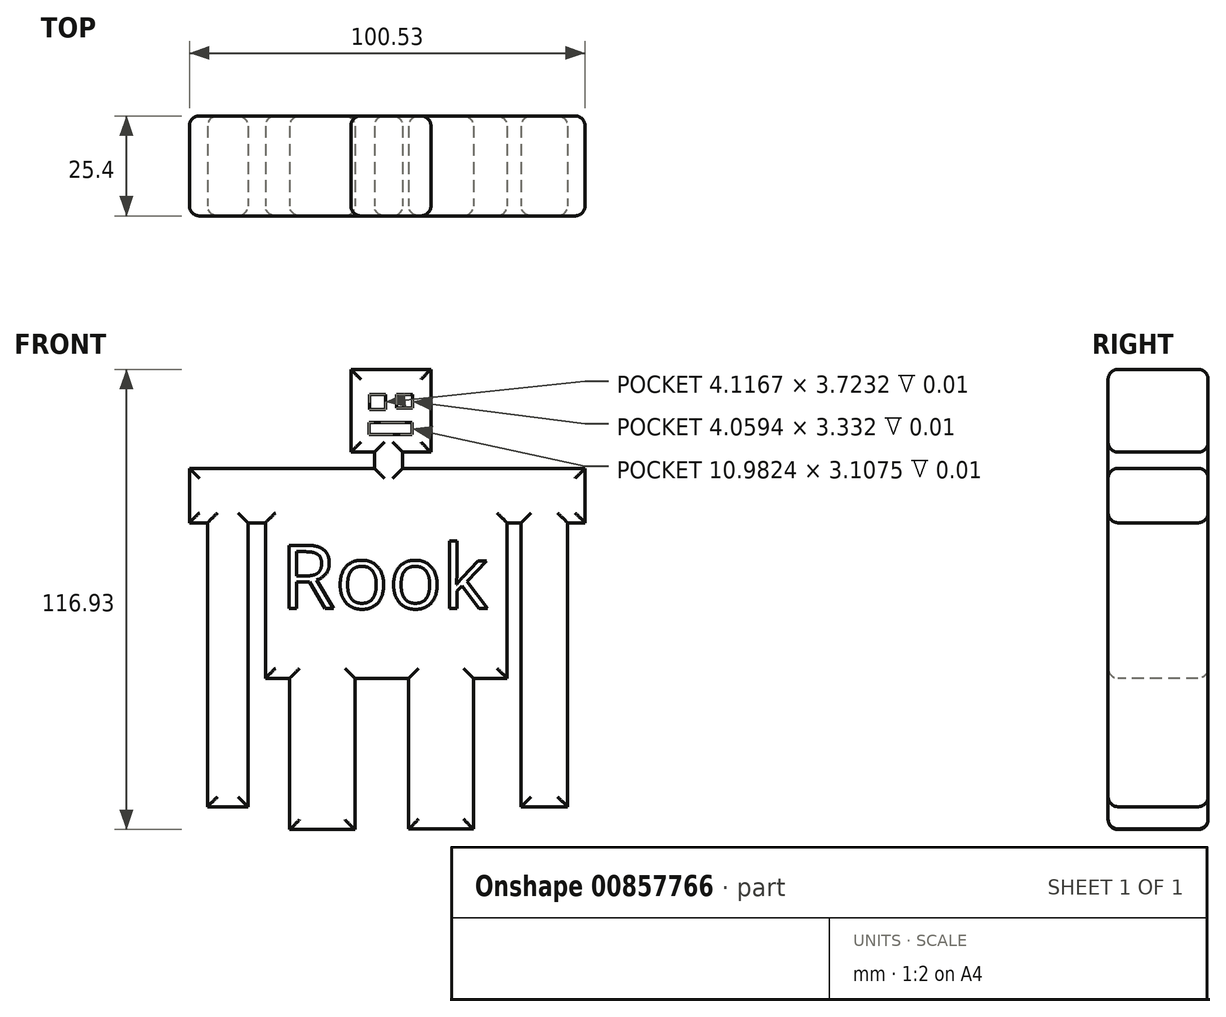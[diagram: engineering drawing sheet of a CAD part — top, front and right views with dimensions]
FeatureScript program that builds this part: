
annotation { "Feature Type Name" : "Feature", "Feature Type Description" : "" }
export const myFeature = defineFeature(function(context is Context, id is Id, definition is map)
    precondition{}
    {
        {
            var Q0;
            Q0=qCreatedBy(makeId("Front.planeOp"),FACE);
            var sketch = newSketch(context, id + "F0", { "sketchPlane" : qUnion([Q0])});
            skLineSegment(sketch, "E0.bottom", {"start": v(-8.8, 63.85) * mm, "end": v(11.54, 63.85) * mm});
            skLineSegment(sketch, "E0.top", {"start": v(-8.8, 42.83) * mm, "end": v(11.54, 42.83) * mm});
            skLineSegment(sketch, "E0.left", {"start": v(-8.8, 63.85) * mm, "end": v(-8.8, 42.83) * mm});
            skLineSegment(sketch, "E0.right", {"start": v(11.54, 63.85) * mm, "end": v(11.54, 42.83) * mm});
            skLineSegment(sketch, "E1.bottom", {"start": v(-2.82, 42.83) * mm, "end": v(4.36, 42.83) * mm});
            skLineSegment(sketch, "E1.top", {"start": v(-2.82, 38.72) * mm, "end": v(4.36, 38.72) * mm});
            skLineSegment(sketch, "E1.left", {"start": v(-2.82, 42.83) * mm, "end": v(-2.82, 38.72) * mm});
            skLineSegment(sketch, "E1.right", {"start": v(4.36, 42.83) * mm, "end": v(4.36, 38.72) * mm});
            skLineSegment(sketch, "E2.bottom", {"start": v(-30.52, 38.72) * mm, "end": v(30.86, 38.72) * mm});
            skLineSegment(sketch, "E2.top", {"start": v(-30.52, -14.62) * mm, "end": v(30.86, -14.62) * mm});
            skLineSegment(sketch, "E2.left", {"start": v(-30.52, 38.72) * mm, "end": v(-30.52, -14.62) * mm});
            skLineSegment(sketch, "E2.right", {"start": v(30.86, 38.72) * mm, "end": v(30.86, -14.62) * mm});
            skLineSegment(sketch, "E3.bottom", {"start": v(30.86, 38.72) * mm, "end": v(50.7, 38.72) * mm});
            skLineSegment(sketch, "E3.top", {"start": v(30.86, 24.87) * mm, "end": v(50.7, 24.87) * mm});
            skLineSegment(sketch, "E3.left", {"start": v(30.86, 38.72) * mm, "end": v(30.86, 24.87) * mm});
            skLineSegment(sketch, "E3.right", {"start": v(50.7, 38.72) * mm, "end": v(50.7, 24.87) * mm});
            skLineSegment(sketch, "E4.bottom", {"start": v(34.45, 24.87) * mm, "end": v(46.25, 24.87) * mm});
            skLineSegment(sketch, "E4.top", {"start": v(34.45, -47.27) * mm, "end": v(46.25, -47.27) * mm});
            skLineSegment(sketch, "E4.left", {"start": v(34.45, 24.87) * mm, "end": v(34.45, -47.27) * mm});
            skLineSegment(sketch, "E4.right", {"start": v(46.25, 24.87) * mm, "end": v(46.25, -47.27) * mm});
            skLineSegment(sketch, "E5.bottom", {"start": v(-30.52, 38.72) * mm, "end": v(-49.84, 38.72) * mm});
            skLineSegment(sketch, "E5.top", {"start": v(-30.52, 24.87) * mm, "end": v(-49.84, 24.87) * mm});
            skLineSegment(sketch, "E5.left", {"start": v(-30.52, 38.72) * mm, "end": v(-30.52, 24.87) * mm});
            skLineSegment(sketch, "E5.right", {"start": v(-49.84, 38.72) * mm, "end": v(-49.84, 24.87) * mm});
            skLineSegment(sketch, "E6.bottom", {"start": v(-45.22, 24.87) * mm, "end": v(-34.96, 24.87) * mm});
            skLineSegment(sketch, "E6.top", {"start": v(-45.22, -47.27) * mm, "end": v(-34.96, -47.27) * mm});
            skLineSegment(sketch, "E6.left", {"start": v(-45.22, 24.87) * mm, "end": v(-45.22, -47.27) * mm});
            skLineSegment(sketch, "E6.right", {"start": v(-34.96, 24.87) * mm, "end": v(-34.96, -47.27) * mm});
            skLineSegment(sketch, "E7.bottom", {"start": v(-24.36, -14.62) * mm, "end": v(-7.78, -14.62) * mm});
            skLineSegment(sketch, "E7.top", {"start": v(-24.36, -53.08) * mm, "end": v(-7.78, -53.08) * mm});
            skLineSegment(sketch, "E7.left", {"start": v(-24.36, -14.62) * mm, "end": v(-24.36, -53.08) * mm});
            skLineSegment(sketch, "E7.right", {"start": v(-7.78, -14.62) * mm, "end": v(-7.78, -53.08) * mm});
            skLineSegment(sketch, "E8.bottom", {"start": v(5.9, -14.62) * mm, "end": v(22.31, -14.62) * mm});
            skLineSegment(sketch, "E8.top", {"start": v(5.9, -52.91) * mm, "end": v(22.31, -52.91) * mm});
            skLineSegment(sketch, "E8.left", {"start": v(5.9, -14.62) * mm, "end": v(5.9, -52.91) * mm});
            skLineSegment(sketch, "E8.right", {"start": v(22.31, -14.62) * mm, "end": v(22.31, -52.91) * mm});
            skSolve(sketch);
        }
        {
            var Q0;
            Q0 = qSketchRegion(id + "F0", true);
            extrude(context, id + "F1", {"entities" : qUnion([Q0]), "oppositeDirection" : true, "depth" : 25.4 * mm, "offsetDistance" : 25.4 * mm});
        }
        {
            var Q0;
            Q0=makeQuery(id+"F1.opExtrude","CAP_EDGE",EDGE,{"disambiguationData":[OSD([sQuery(id+"F0.wireOp",EDGE,"E0.bottom")])],"isStart":true});
            var Q1;
            Q1=makeQuery(id+"F1.opExtrude","CAP_EDGE",EDGE,{"disambiguationData":[OSD([sQuery(id+"F0.wireOp",EDGE,"E0.left")])],"isStart":true});
            var Q2;
            Q2=makeQuery(id+"F1.opExtrude","CAP_FACE",FACE,{"disambiguationData":[OSD([sQuery(id+"F0.wireOp",EDGE,"E0.bottom"),sQuery(id+"F0.wireOp",EDGE,"E0.top"),sQuery(id+"F0.wireOp",EDGE,"E0.left"),sQuery(id+"F0.wireOp",EDGE,"E0.right"),sQuery(id+"F0.wireOp",EDGE,"E1.left"),sQuery(id+"F0.wireOp",EDGE,"E1.right"),sQuery(id+"F0.wireOp",EDGE,"E2.bottom"),sQuery(id+"F0.wireOp",EDGE,"E2.top"),sQuery(id+"F0.wireOp",EDGE,"E2.left"),sQuery(id+"F0.wireOp",EDGE,"E2.right"),sQuery(id+"F0.wireOp",EDGE,"E3.bottom"),sQuery(id+"F0.wireOp",EDGE,"E3.top"),sQuery(id+"F0.wireOp",EDGE,"E3.right"),sQuery(id+"F0.wireOp",EDGE,"E4.top"),sQuery(id+"F0.wireOp",EDGE,"E4.left"),sQuery(id+"F0.wireOp",EDGE,"E4.right"),sQuery(id+"F0.wireOp",EDGE,"E5.bottom"),sQuery(id+"F0.wireOp",EDGE,"E5.top"),sQuery(id+"F0.wireOp",EDGE,"E5.right"),sQuery(id+"F0.wireOp",EDGE,"E6.top"),sQuery(id+"F0.wireOp",EDGE,"E6.left"),sQuery(id+"F0.wireOp",EDGE,"E6.right"),sQuery(id+"F0.wireOp",EDGE,"E7.top"),sQuery(id+"F0.wireOp",EDGE,"E7.left"),sQuery(id+"F0.wireOp",EDGE,"E7.right"),sQuery(id+"F0.wireOp",EDGE,"E8.top"),sQuery(id+"F0.wireOp",EDGE,"E8.left"),sQuery(id+"F0.wireOp",EDGE,"E8.right")])],"isStart":true});
            var Q3;
            Q3=makeQuery(id+"F1.opExtrude","CAP_EDGE",EDGE,{"disambiguationData":[OSD([sQuery(id+"F0.wireOp",EDGE,"E0.right")])],"isStart":false});
            var Q4;
            Q4=makeQuery(id+"F1.opExtrude","CAP_EDGE",EDGE,{"disambiguationData":[OSD([sQuery(id+"F0.wireOp",EDGE,"E0.left")])],"isStart":false});
            var Q5;
            Q5=makeQuery(id+"F1.opExtrude","CAP_EDGE",EDGE,{"disambiguationData":[OSD([sQuery(id+"F0.wireOp",EDGE,"E0.bottom")])],"isStart":false});
            var Q6;
            Q6=makeQuery(id+"F1.opExtrude","CAP_EDGE",EDGE,{"disambiguationData":[OSD([sQuery(id+"F0.wireOp",EDGE,"E2.bottom"),sQuery(id+"F0.wireOp",EDGE,"E3.bottom")])],"isStart":false});
            var Q7;
            Q7=makeQuery(id+"F1.opExtrude","CAP_EDGE",EDGE,{"disambiguationData":[OSD([sQuery(id+"F0.wireOp",EDGE,"E3.right")])],"isStart":false});
            var Q8;
            {var subQ0=sQuery(id+"F0.wireOp",EDGE,"E3.top");Q8=makeQuery(id+"F1.opExtrude","CAP_EDGE",EDGE,{"disambiguationData":[OSD([subQ0]),TDD([makeQuery(id+"F0.imprint","IMPRINT",EDGE,{"disambiguationData":[TD([[makeQuery(id+"F0.imprint","INTERSECT",VERTEX,{"derivedFrom":[subQ0,sQuery(id+"F0.wireOp",EDGE,"E3.right")]}),1.0]])],"derivedFrom":subQ0})])],"isStart":false});}
            var Q9;
            Q9=makeQuery(id+"F1.opExtrude","CAP_EDGE",EDGE,{"disambiguationData":[OSD([sQuery(id+"F0.wireOp",EDGE,"E4.right")])],"isStart":false});
            var Q10;
            Q10=makeQuery(id+"F1.opExtrude","CAP_EDGE",EDGE,{"disambiguationData":[OSD([sQuery(id+"F0.wireOp",EDGE,"E4.top")])],"isStart":false});
            var Q11;
            Q11=makeQuery(id+"F1.opExtrude","CAP_EDGE",EDGE,{"disambiguationData":[OSD([sQuery(id+"F0.wireOp",EDGE,"E4.left")])],"isStart":false});
            var Q12;
            {var subQ0=sQuery(id+"F0.wireOp",EDGE,"E3.top");Q12=makeQuery(id+"F1.opExtrude","CAP_EDGE",EDGE,{"disambiguationData":[OSD([subQ0]),TDD([makeQuery(id+"F0.imprint","IMPRINT",EDGE,{"disambiguationData":[TD([[makeQuery(id+"F0.imprint","INTERSECT",VERTEX,{"derivedFrom":[sQuery(id+"F0.wireOp",EDGE,"E2.right"),subQ0,sQuery(id+"F0.wireOp",EDGE,"E3.left")]}),-1.0]])],"derivedFrom":subQ0})])],"isStart":false});}
            var Q13;
            Q13=makeQuery(id+"F1.opExtrude","CAP_EDGE",EDGE,{"disambiguationData":[OSD([sQuery(id+"F0.wireOp",EDGE,"E2.right")])],"isStart":false});
            var Q14;
            Q14=makeQuery(id+"F1.opExtrude","CAP_EDGE",EDGE,{"disambiguationData":[OSD([sQuery(id+"F0.wireOp",EDGE,"E8.right")])],"isStart":false});
            var Q15;
            Q15=makeQuery(id+"F1.opExtrude","CAP_EDGE",EDGE,{"disambiguationData":[OSD([sQuery(id+"F0.wireOp",EDGE,"E8.top")])],"isStart":false});
            var Q16;
            Q16=makeQuery(id+"F1.opExtrude","CAP_EDGE",EDGE,{"disambiguationData":[OSD([sQuery(id+"F0.wireOp",EDGE,"E8.left")])],"isStart":false});
            var Q17;
            Q17=makeQuery(id+"F1.opExtrude","CAP_EDGE",EDGE,{"disambiguationData":[OSD([sQuery(id+"F0.wireOp",EDGE,"E7.right")])],"isStart":true});
            var Q18;
            Q18=makeQuery(id+"F1.opExtrude","CAP_EDGE",EDGE,{"disambiguationData":[OSD([sQuery(id+"F0.wireOp",EDGE,"E7.top")])],"isStart":false});
            var Q19;
            Q19=makeQuery(id+"F1.opExtrude","CAP_EDGE",EDGE,{"disambiguationData":[OSD([sQuery(id+"F0.wireOp",EDGE,"E7.left")])],"isStart":false});
            var Q20;
            {var subQ0=sQuery(id+"F0.wireOp",EDGE,"E2.top");Q20=makeQuery(id+"F1.opExtrude","CAP_EDGE",EDGE,{"disambiguationData":[OSD([subQ0]),TDD([makeQuery(id+"F0.imprint","IMPRINT",EDGE,{"disambiguationData":[TD([[makeQuery(id+"F0.imprint","INTERSECT",VERTEX,{"derivedFrom":[subQ0,sQuery(id+"F0.wireOp",EDGE,"E2.left")]}),-1.0]])],"derivedFrom":subQ0})])],"isStart":false});}
            var Q21;
            Q21=makeQuery(id+"F1.opExtrude","CAP_EDGE",EDGE,{"disambiguationData":[OSD([sQuery(id+"F0.wireOp",EDGE,"E2.left")])],"isStart":false});
            var Q22;
            {var subQ0=sQuery(id+"F0.wireOp",EDGE,"E5.top");Q22=makeQuery(id+"F1.opExtrude","CAP_EDGE",EDGE,{"disambiguationData":[OSD([subQ0]),TDD([makeQuery(id+"F0.imprint","IMPRINT",EDGE,{"disambiguationData":[TD([[makeQuery(id+"F0.imprint","INTERSECT",VERTEX,{"derivedFrom":[sQuery(id+"F0.wireOp",EDGE,"E2.left"),subQ0,sQuery(id+"F0.wireOp",EDGE,"E5.left")]}),-1.0]])],"derivedFrom":subQ0})])],"isStart":false});}
            var Q23;
            Q23=makeQuery(id+"F1.opExtrude","CAP_EDGE",EDGE,{"disambiguationData":[OSD([sQuery(id+"F0.wireOp",EDGE,"E6.right")])],"isStart":true});
            var Q24;
            Q24=makeQuery(id+"F1.opExtrude","CAP_EDGE",EDGE,{"disambiguationData":[OSD([sQuery(id+"F0.wireOp",EDGE,"E6.top")])],"isStart":false});
            var Q25;
            Q25=makeQuery(id+"F1.opExtrude","CAP_EDGE",EDGE,{"disambiguationData":[OSD([sQuery(id+"F0.wireOp",EDGE,"E6.left")])],"isStart":false});
            var Q26;
            Q26=makeQuery(id+"F1.opExtrude","CAP_EDGE",EDGE,{"disambiguationData":[OSD([sQuery(id+"F0.wireOp",EDGE,"E1.left")])],"isStart":false});
            var Q27;
            Q27=makeQuery(id+"F1.opExtrude","CAP_EDGE",EDGE,{"disambiguationData":[OSD([sQuery(id+"F0.wireOp",EDGE,"E2.bottom"),sQuery(id+"F0.wireOp",EDGE,"E5.bottom")])],"isStart":false});
            var Q28;
            Q28=makeQuery(id+"F1.opExtrude","CAP_EDGE",EDGE,{"disambiguationData":[OSD([sQuery(id+"F0.wireOp",EDGE,"E6.right")])],"isStart":false});
            var Q29;
            Q29=makeQuery(id+"F1.opExtrude","CAP_EDGE",EDGE,{"disambiguationData":[OSD([sQuery(id+"F0.wireOp",EDGE,"E7.right")])],"isStart":false});
            var Q30;
            {var subQ0=sQuery(id+"F0.wireOp",EDGE,"E2.top");Q30=makeQuery(id+"F1.opExtrude","CAP_EDGE",EDGE,{"disambiguationData":[OSD([subQ0]),TDD([makeQuery(id+"F0.imprint","IMPRINT",EDGE,{"disambiguationData":[TD([[makeQuery(id+"F0.imprint","INTERSECT",VERTEX,{"derivedFrom":[subQ0,sQuery(id+"F0.wireOp",EDGE,"E2.right")]}),1.0]])],"derivedFrom":subQ0})])],"isStart":false});}
            var Q31;
            {var subQ0=sQuery(id+"F0.wireOp",EDGE,"E2.top");Q31=makeQuery(id+"F1.opExtrude","CAP_EDGE",EDGE,{"disambiguationData":[OSD([subQ0]),TDD([makeQuery(id+"F0.imprint","IMPRINT",EDGE,{"disambiguationData":[TD([[makeQuery(id+"F0.imprint","INTERSECT",VERTEX,{"derivedFrom":[subQ0,sQuery(id+"F0.wireOp",EDGE,"E7.bottom"),sQuery(id+"F0.wireOp",EDGE,"E7.right")]}),-1.0]])],"derivedFrom":subQ0})])],"isStart":false});}
            var Q32;
            Q32=makeQuery(id+"F1.opExtrude","CAP_EDGE",EDGE,{"disambiguationData":[OSD([sQuery(id+"F0.wireOp",EDGE,"E5.right")])],"isStart":false});
            var Q33;
            Q33=makeQuery(id+"F1.opExtrude","CAP_EDGE",EDGE,{"disambiguationData":[OSD([sQuery(id+"F0.wireOp",EDGE,"E1.right")])],"isStart":false});
            var Q34;
            {var subQ0=sQuery(id+"F0.wireOp",EDGE,"E5.top");Q34=makeQuery(id+"F1.opExtrude","CAP_EDGE",EDGE,{"disambiguationData":[OSD([subQ0]),TDD([makeQuery(id+"F0.imprint","IMPRINT",EDGE,{"disambiguationData":[TD([[makeQuery(id+"F0.imprint","INTERSECT",VERTEX,{"derivedFrom":[subQ0,sQuery(id+"F0.wireOp",EDGE,"E5.right")]}),1.0]])],"derivedFrom":subQ0})])],"isStart":false});}
            var Q35;
            {var subQ0=sQuery(id+"F0.wireOp",EDGE,"E0.top");Q35=makeQuery(id+"F1.opExtrude","CAP_EDGE",EDGE,{"disambiguationData":[OSD([subQ0]),TDD([makeQuery(id+"F0.imprint","IMPRINT",EDGE,{"disambiguationData":[TD([[makeQuery(id+"F0.imprint","INTERSECT",VERTEX,{"derivedFrom":[subQ0,sQuery(id+"F0.wireOp",EDGE,"E0.right")]}),1.0]])],"derivedFrom":subQ0})])],"isStart":false});}
            var Q36;
            {var subQ0=sQuery(id+"F0.wireOp",EDGE,"E0.top");Q36=makeQuery(id+"F1.opExtrude","CAP_EDGE",EDGE,{"disambiguationData":[OSD([subQ0]),TDD([makeQuery(id+"F0.imprint","IMPRINT",EDGE,{"disambiguationData":[TD([[makeQuery(id+"F0.imprint","INTERSECT",VERTEX,{"derivedFrom":[subQ0,sQuery(id+"F0.wireOp",EDGE,"E0.left")]}),-1.0]])],"derivedFrom":subQ0})])],"isStart":false});}
            fillet(context, id + "F2", {"entities" : qUnion([Q0, Q1, Q2, Q3, Q4, Q5, Q6, Q7, Q8, Q9, Q10, Q11, Q12, Q13, Q14, Q15, Q16, Q17, Q18, Q19, Q20, Q21, Q22, Q23, Q24, Q25, Q26, Q27, Q28, Q29, Q30, Q31, Q32, Q33, Q34, Q35, Q36]), "radius" : 2.54 * mm, "tangentPropagation" : true, "allowEdgeOverflow" : false});
        }
        {
            var Q0;
            Q0=qCreatedBy(makeId("Front.planeOp"),FACE);
            var sketch = newSketch(context, id + "F3", { "sketchPlane" : qUnion([Q0])});
            skText(sketch, "E9", { "text": "Rook", "fontName": "OpenSans-Regular.ttf"});
            const initialGuessF3  = {"E9": [-0.02669, 0.00311, 1, 0, 0.01619]};
            skSetInitialGuess(sketch, initialGuessF3);
            skSolve(sketch);
        }
        {
            var Q0;
            Q0 = qSketchRegion(id + "F3", true);
            extrude(context, id + "F4", {"entities" : qUnion([Q0]), "operationType" : NewBodyOperationType.REMOVE, "oppositeDirection" : true, "depth" : 1 / 101.6 * mm, "offsetDistance" : 25.4 * mm});
        }
        {
            var Q0;
            Q0=qCreatedBy(makeId("Front.planeOp"),FACE);
            var sketch = newSketch(context, id + "F5", { "sketchPlane" : qUnion([Q0])});
            skLineSegment(sketch, "E10.bottom", {"start": v(-4.12, 57.42) * mm, "end": v(0, 57.42) * mm});
            skLineSegment(sketch, "E10.top", {"start": v(-4.12, 53.7) * mm, "end": v(0, 53.7) * mm});
            skLineSegment(sketch, "E10.left", {"start": v(-4.12, 57.42) * mm, "end": v(-4.12, 53.7) * mm});
            skLineSegment(sketch, "E10.right", {"start": v(0, 57.42) * mm, "end": v(0, 53.7) * mm});
            skLineSegment(sketch, "E11.bottom", {"start": v(6.82, 57.42) * mm, "end": v(2.76, 57.42) * mm});
            skLineSegment(sketch, "E11.top", {"start": v(6.82, 54.08) * mm, "end": v(2.76, 54.08) * mm});
            skLineSegment(sketch, "E11.left", {"start": v(6.82, 57.42) * mm, "end": v(6.82, 54.08) * mm});
            skLineSegment(sketch, "E11.right", {"start": v(2.76, 57.42) * mm, "end": v(2.76, 54.08) * mm});
            skLineSegment(sketch, "E12.bottom", {"start": v(-4.2, 50.4) * mm, "end": v(6.78, 50.4) * mm});
            skLineSegment(sketch, "E12.top", {"start": v(-4.2, 47.3) * mm, "end": v(6.78, 47.3) * mm});
            skLineSegment(sketch, "E12.left", {"start": v(-4.2, 50.4) * mm, "end": v(-4.2, 47.3) * mm});
            skLineSegment(sketch, "E12.right", {"start": v(6.78, 50.4) * mm, "end": v(6.78, 47.3) * mm});
            skSolve(sketch);
        }
        {
            var Q0;
            Q0 = qSketchRegion(id + "F5", true);
            extrude(context, id + "F6", {"entities" : qUnion([Q0]), "operationType" : NewBodyOperationType.REMOVE, "oppositeDirection" : true, "depth" : 1 / 101.6 * mm, "offsetDistance" : 25.4 * mm});
        }
    });
